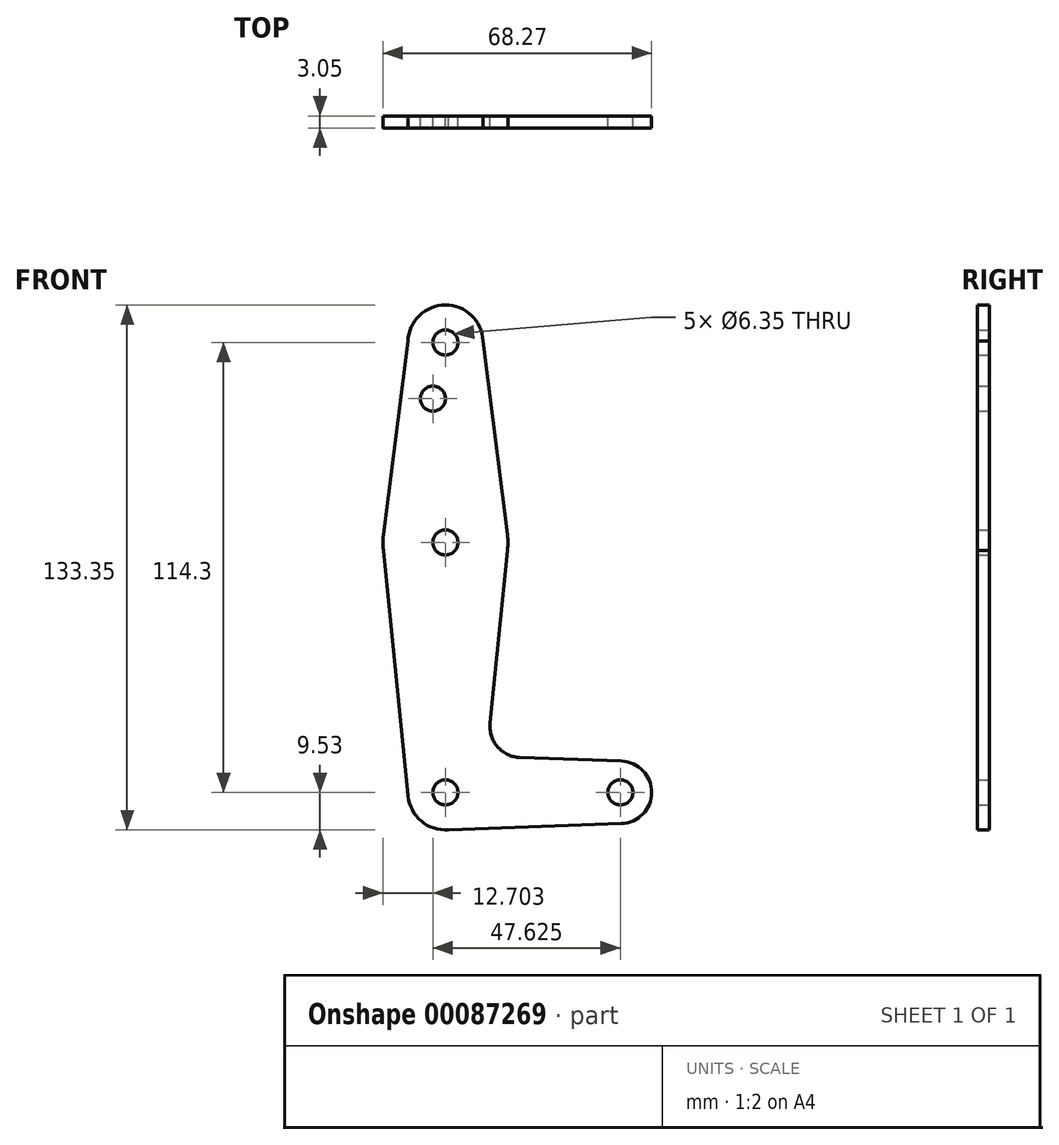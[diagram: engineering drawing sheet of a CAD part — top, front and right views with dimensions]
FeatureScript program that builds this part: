
annotation { "Feature Type Name" : "Feature", "Feature Type Description" : "" }
export const myFeature = defineFeature(function(context is Context, id is Id, definition is map)
    precondition{}
    {
        {
            var Q0;
            Q0=qCreatedBy(makeId("Front.planeOp"),FACE);
            var sketch = newSketch(context, id + "F0", { "sketchPlane" : qUnion([Q0])});
            skLineSegment(sketch, "E0", {"start": v(-46.87, 61.49) * mm, "end": v(-46.87, -52.81) * mm});
            skLineSegment(sketch, "E1", {"start": v(-46.87, -52.81) * mm, "end": v(-2.42, -52.81) * mm});
            skCircle(sketch, "E2", {"center": v(-2.42, -52.81) * mm, "radius": 7.94 * mm});
            skCircle(sketch, "E3", {"center": v(-46.87, -52.81) * mm, "radius": 9.53 * mm});
            skCircle(sketch, "E4", {"center": v(-46.87, 61.49) * mm, "radius": 9.53 * mm});
            skCircle(sketch, "E5", {"center": v(-46.87, 10.69) * mm, "radius": 15.88 * mm});
            skLineSegment(sketch, "E6", {"start": v(-56.4, 61.83) * mm, "end": v(-62.62, 12.69) * mm});
            skLineSegment(sketch, "E7", {"start": v(-62.62, 8.7) * mm, "end": v(-56.35, -53.76) * mm});
            skLineSegment(sketch, "E8", {"start": v(-46.95, -62.33) * mm, "end": v(-2.14, -60.74) * mm});
            skLineSegment(sketch, "E9", {"start": v(-27.9, -43.96) * mm, "end": v(-2.14, -44.88) * mm});
            skLineSegment(sketch, "E10", {"start": v(-37.35, 61.85) * mm, "end": v(-31.12, 12.69) * mm});
            skLineSegment(sketch, "E11", {"start": v(-31.12, 8.7) * mm, "end": v(-35.53, -35.22) * mm});
            skCircle(sketch, "E12", {"center": v(-46.87, 61.49) * mm, "radius": 3.18 * mm});
            skCircle(sketch, "E13", {"center": v(-46.87, 10.69) * mm, "radius": 3.18 * mm});
            skCircle(sketch, "E14", {"center": v(-46.87, -52.81) * mm, "radius": 3.18 * mm});
            skCircle(sketch, "E15", {"center": v(-2.42, -52.81) * mm, "radius": 3.18 * mm});
            skCircle(sketch, "E16", {"center": v(-50.05, 47.22) * mm, "radius": 3.18 * mm});
            skArc(sketch, "E17.filletArc", {"start": v(-35.53, -35.22) * mm, "mid": v(-33.61, -41.24) * mm, "end": v(-27.9, -43.96) * mm});
            skSolve(sketch);
        }
        {
            var Q0;
            Q0 = qSketchRegion(id + "F0", true);
            var Q1;
            {var subQ0=sQuery(id+"F0.wireOp",EDGE,"E3");var subQ1=sQuery(id+"F0.wireOp",EDGE,"E0");var subQ2=makeQuery(id+"F0.imprint","INTERSECT",VERTEX,{"derivedFrom":[subQ1,subQ0]});Q1=makeQuery(id+"F0.imprint","IMPRINT",FACE,{"disambiguationData":[TD([[makeQuery(id+"F0.imprint","IMPRINT",EDGE,{"disambiguationData":[TD([[subQ2,-1.0]])],"derivedFrom":subQ1}),1.0]])]});}
            extrude(context, id + "F1", {"entities" : qUnion([Q0, Q1]), "depth" : 3.05 * mm});
        }
    });
